# Revit family: Theater-Curtains
name_source: partatom
category: Specialty Equipment
units: mm (PartAtom-declared; Revit-internal decimal feet)

## family parameters
Always vertical = Yes
Classification Number = 23.40.50.14
Cut with Voids When Loaded = No
Enable Cutting in Views = No
Maintain Annotation Orientation = No
Part Type = Normal
Room Calculation Point = No
Round Connector Dimension = Use Diameter
Shared = No
Work Plane-Based = No

## types (1)
- ByType
    Assembly Code = E1020330
    Carrier Spacing - oc = 1' - 0"
    Carrier Type = 4-wheel assemblies with formed steel bodies and two swivel hooks
    Construction Details = http://www.arcat.com
    Curtain Fabric = ARCAT - Textiles - Velour - 25oz Cotton - Burgundy
    Default Elevation = 0' - 0"
    Depth = 0' - 4"
    Description = Velour Stage Curtains
    Expected Lifespan (Years) = 25
    Green Building-LEED = http://www.arcat.com
    Height = 11' - 0"
    Keynote = 11060
    Length = 12' - 0"
    Maintenance Schedule (Months) = 6
    Manufacturer = Generic
    Manufacturer Fax = (203) 939-2444
    Manufacturer Website = http://www.arcat.com
    Model = Generic
    Operating Line = 1/4" diameter, stretch-resistant rope with spun polyester outer jacket double braided over solid polyester core
    Product Data = http://www.arcat.com
    Product Properties = http://www.arcat.com
    Specification = http://www.arcat.com
    Track System = Heavy Dudty Straight Track w/ Carriers
    Warranty Duration (Years) = 2

## geometry (parser evidence)
native form markers: Sweep x1
no freeform markers — native parametric forms only
